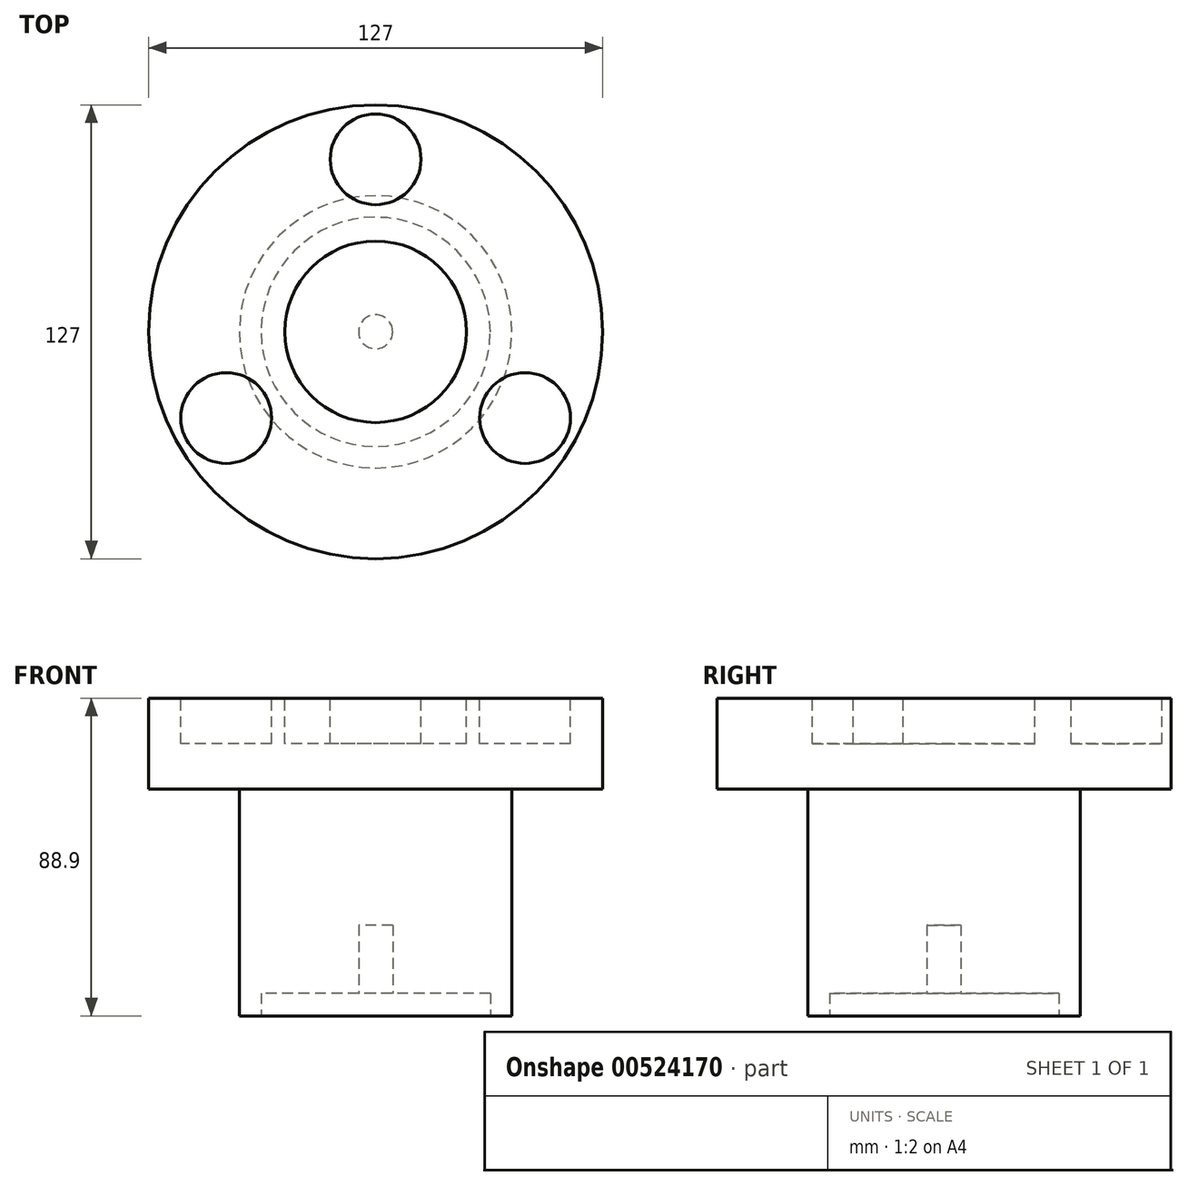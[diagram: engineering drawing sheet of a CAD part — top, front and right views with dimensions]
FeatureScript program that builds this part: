
annotation { "Feature Type Name" : "Feature", "Feature Type Description" : "" }
export const myFeature = defineFeature(function(context is Context, id is Id, definition is map)
    precondition{}
    {
        {
            var Q0;
            Q0=qCreatedBy(makeId("Top.planeOp"),FACE);
            var sketch = newSketch(context, id + "F0", { "sketchPlane" : qUnion([Q0])});
            skCircle(sketch, "E0", {"center": v(0, 0) * mm, "radius": 38.1 * mm});
            skCircle(sketch, "E1", {"center": v(0, 0) * mm, "radius": 32.07 * mm});
            skSolve(sketch);
        }
        {
            var Q0;
            Q0=qSketchRegion(id+"F0",true);
            var Q1;
            Q1=makeQuery(id+"F0.imprint","IMPRINT",FACE,{"disambiguationData":[TD([[makeQuery(id+"F0.imprint","IMPRINT",EDGE,{"derivedFrom":sQuery(id+"F0.wireOp",EDGE,"E1")}),1.0]])]});
            extrude(context, id + "F1", {"entities" : qUnion([Q0, Q1]), "depth" : 63.5 * mm});
        }
        {
            var Q0;
            Q0=makeQuery(id+"F0.imprint","IMPRINT",FACE,{"disambiguationData":[TD([[makeQuery(id+"F0.imprint","IMPRINT",EDGE,{"derivedFrom":sQuery(id+"F0.wireOp",EDGE,"E1")}),1.0]])]});
            extrude(context, id + "F2", {"entities" : qUnion([Q0]), "operationType" : NewBodyOperationType.REMOVE, "depth" : 6.35 * mm});
        }
        {
            var Q0;
            Q0=qCreatedBy(makeId("Top.planeOp"),FACE);
            var sketch = newSketch(context, id + "F3", { "sketchPlane" : qUnion([Q0])});
            skCircle(sketch, "E2", {"center": v(0, 0) * mm, "radius": 4.76 * mm});
            skSolve(sketch);
        }
        {
            var Q0;
            Q0=qSketchRegion(id+"F3",true);
            extrude(context, id + "F4", {"entities" : qUnion([Q0]), "operationType" : NewBodyOperationType.REMOVE, "depth" : 25.4 * mm});
        }
        {
            var Q0;
            Q0=makeQuery(id+"F1.opExtrude","CAP_FACE",FACE,{"disambiguationData":[OSD([sQuery(id+"F0.wireOp",EDGE,"E0")])],"isStart":false});
            var sketch = newSketch(context, id + "F5", { "sketchPlane" : qUnion([Q0])});
            skCircle(sketch, "E3", {"center": v(0, 0) * mm, "radius": 63.5 * mm});
            skSolve(sketch);
        }
        {
            var Q0;
            Q0=qSketchRegion(id+"F5",true);
            extrude(context, id + "F6", {"entities" : qUnion([Q0]), "operationType" : NewBodyOperationType.ADD, "depth" : 25.4 * mm});
        }
        {
            var Q0;
            Q0=makeQuery(id+"F6.opExtrude","CAP_FACE",FACE,{"disambiguationData":[OSD([sQuery(id+"F5.wireOp",EDGE,"E3")])],"isStart":false});
            var sketch = newSketch(context, id + "F7", { "sketchPlane" : qUnion([Q0])});
            skCircle(sketch, "E4", {"center": v(0, 48.26) * mm, "radius": 12.7 * mm});
            skCircle(sketch, "E5.1.0", {"center": v(-41.8, -24.13) * mm, "radius": 12.7 * mm});
            skCircle(sketch, "E5.2.0", {"center": v(41.8, -24.13) * mm, "radius": 12.7 * mm});
            skPoint(sketch, "E5.center", {"position": v(0, 0) * mm});
            skCircle(sketch, "E6", {"center": v(0, 0) * mm, "radius": 25.4 * mm});
            skSolve(sketch);
        }
        {
            var Q0;
            Q0=qSketchRegion(id+"F7",true);
            extrude(context, id + "F8", {"entities" : qUnion([Q0]), "operationType" : NewBodyOperationType.REMOVE, "oppositeDirection" : true, "depth" : 12.7 * mm});
        }
    });
